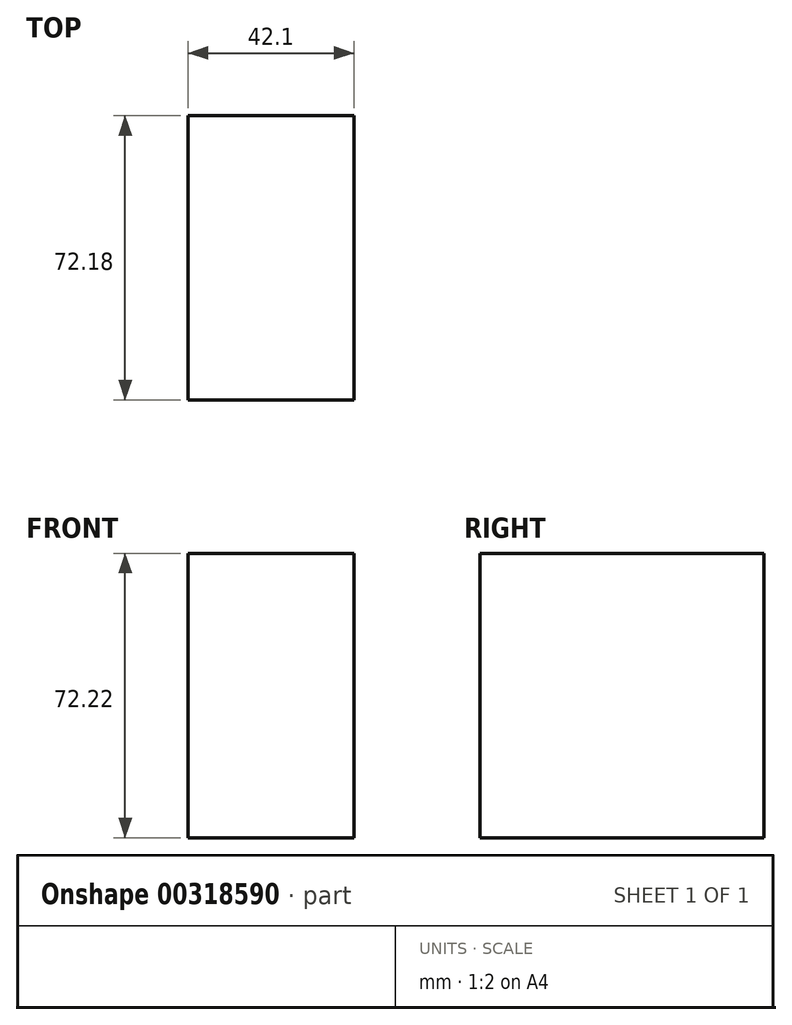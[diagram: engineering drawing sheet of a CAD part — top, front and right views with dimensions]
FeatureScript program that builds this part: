
annotation { "Feature Type Name" : "Feature", "Feature Type Description" : "" }
export const myFeature = defineFeature(function(context is Context, id is Id, definition is map)
    precondition{}
    {
        {
            var Q0;
            Q0=qCreatedBy(makeId("Front.planeOp"),FACE);
            var sketch = newSketch(context, id + "F0", { "sketchPlane" : qUnion([Q0])});
            skLineSegment(sketch, "E0.bottom", {"start": v(-27.3, 54.6) * mm, "end": v(14.8, 54.6) * mm});
            skLineSegment(sketch, "E0.top", {"start": v(-27.3, -17.62) * mm, "end": v(14.8, -17.62) * mm});
            skLineSegment(sketch, "E0.left", {"start": v(-27.3, 54.6) * mm, "end": v(-27.3, -17.62) * mm});
            skLineSegment(sketch, "E0.right", {"start": v(14.8, 54.6) * mm, "end": v(14.8, -17.62) * mm});
            skSolve(sketch);
        }
        {
            var Q0;
            Q0 = qSketchRegion(id + "F0", true);
            extrude(context, id + "F1", {"entities" : qUnion([Q0]), "depth" : 72.18 * mm});
        }
    });
